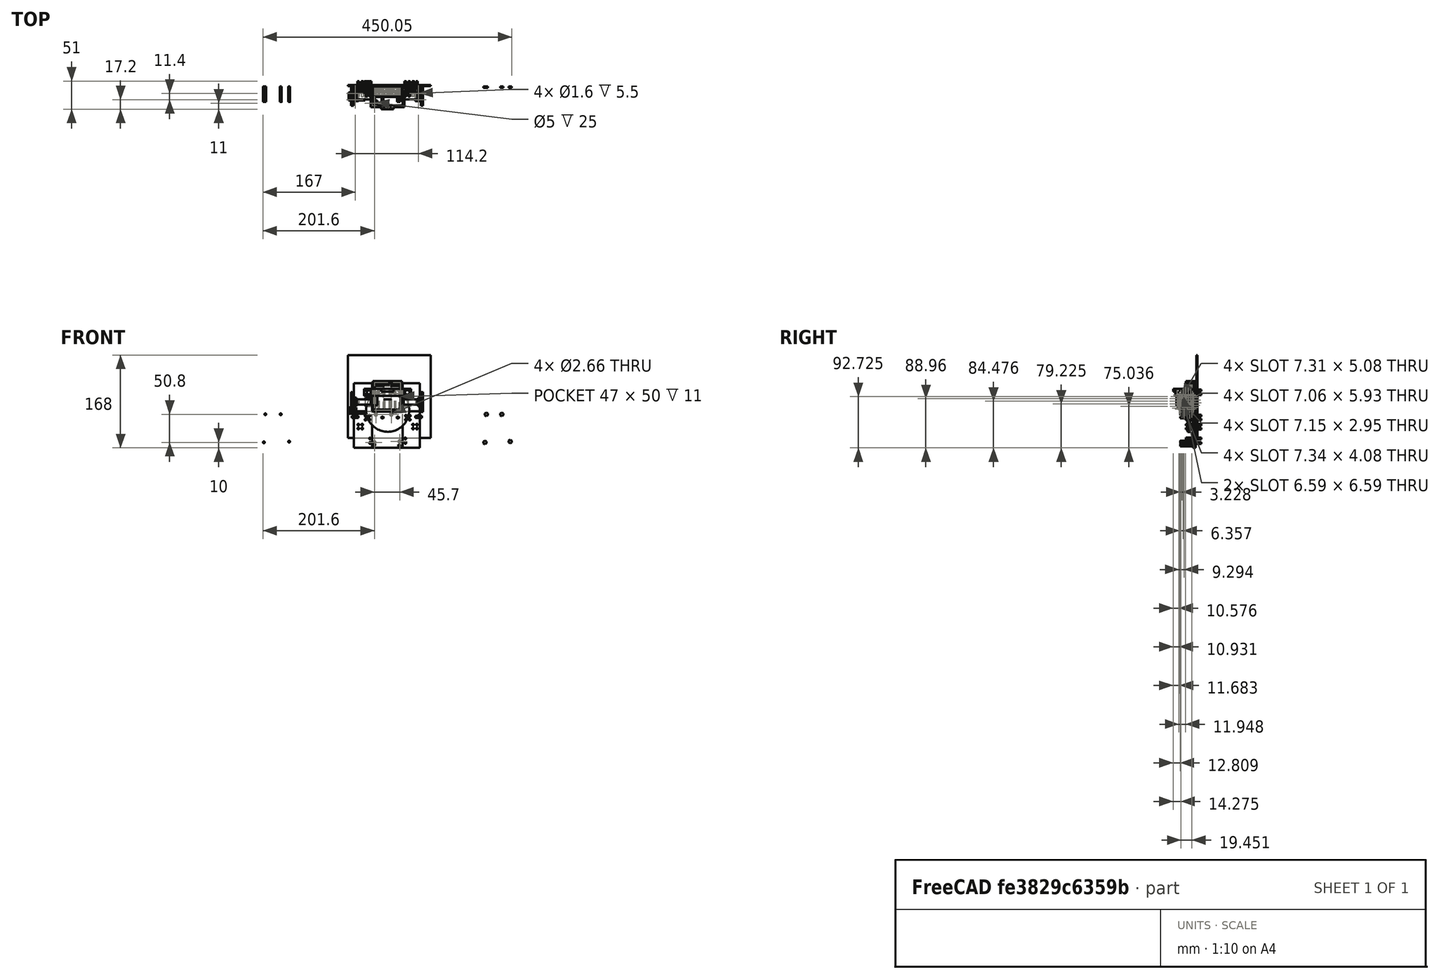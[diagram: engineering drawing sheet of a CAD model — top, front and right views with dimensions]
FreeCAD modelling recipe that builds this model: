
FCSTD DOCUMENT  (FreeCAD 0.16R6712 (Git))
Label: 5028.2 Blank Frank the Robot
License: All rights reserved
LicenseURL: http://en.wikipedia.org/wiki/All_rights_reserved
objects: Part::Cylinder×83, Part::Box×45, Part::Fuse×45, Part::Cut×39, Part::Feature×17, Part::MultiFuse×16, Part::Mirroring×6, Part::Cone×4, Part::Compound×3, Part::Torus×2, Part::Chamfer×2, App::DocumentObjectGroup×1
note: 262 computed .brp shape members not serialized (recipe doc carries the construction recipe); baked Part::Feature solids carry a one-line shape summary decoded from their .brp

FEATURE [Part::Cylinder] Cylinder
  Angle = 360
  Height = 30
  Radius = 7
FEATURE [Part::Cylinder] Cylinder001
  Angle = 360
  Height = 19
  Placement = pos=(0,0,30) rot=(0,0,1;0rad)
  Radius = 7
FEATURE [Part::Cylinder] Cylinder002
  Angle = 360
  Height = 1.8
  Placement = pos=(0,0,49) rot=(0,0,1;0rad)
  Radius = 2.5
FEATURE [Part::Compound] Compound
  Links = -> [Cylinder,Cylinder002,Cylinder001]
FEATURE [Part::Cylinder] Cylinder003
  Angle = 360
  Height = 30
  Radius = 7
FEATURE [Part::Cylinder] Cylinder004
  Angle = 360
  Height = 19
  Placement = pos=(0,0,30) rot=(0,0,1;0rad)
  Radius = 7
FEATURE [Part::Cylinder] Cylinder005
  Angle = 360
  Height = 1.8
  Placement = pos=(0,0,49) rot=(0,0,1;0rad)
  Radius = 2.5
FEATURE [Part::Compound] Compound001
  Links = -> [Cylinder003,Cylinder005,Cylinder004]
  Placement = pos=(14.5,0,50) rot=(1,0,0;3.14159rad)
FEATURE [Part::Cylinder] Cylinder006
  Angle = 360
  Height = 30
  Radius = 7
FEATURE [Part::Cylinder] Cylinder007
  Angle = 360
  Height = 19
  Placement = pos=(0,0,30) rot=(0,0,1;0rad)
  Radius = 7
FEATURE [Part::Cylinder] Cylinder008
  Angle = 360
  Height = 1.8
  Placement = pos=(0,0,49) rot=(0,0,1;0rad)
  Radius = 2.5
FEATURE [Part::Compound] Compound002
  Links = -> [Cylinder006,Cylinder008,Cylinder007]
  Placement = pos=(29,0,0) rot=(0,0,1;0rad)
FEATURE [Part::Box] Box  label="Cube"
  Height = 50
  Length = 47
  Placement = pos=(-9,-8,0) rot=(0,0,1;0rad)
  Width = 12
FEATURE [Part::Box] Box001  label="Cube001"
  Height = 55
  Length = 53
  Placement = pos=(-12,-8,-2.5) rot=(0,0,1;0rad)
  Width = 11
FEATURE [Part::Cylinder] Cylinder009
  Angle = 360
  Height = 50
  Radius = 7
FEATURE [Part::Cylinder] Cylinder010
  Angle = 360
  Height = 50
  Placement = pos=(14.5,0,0) rot=(0,0,1;0rad)
  Radius = 7
FEATURE [Part::Cut] Cut
  Base = -> Box001
  Tool = -> Box
FEATURE [Part::Box] Box002  label="Cube002"
  Height = 55
  Length = 53
  Placement = pos=(-12,3,-2.5) rot=(0,0,1;0rad)
  Width = 7
FEATURE [Part::Fuse] Fusion
  Base = -> Cut
  Tool = -> Box002
FEATURE [Part::Cut] Cut001  label="No idea why this is here...."
  Base = -> Fusion
  Tool = -> Cylinder009
FEATURE [Part::Cylinder] Cylinder011
  Angle = 360
  Height = 50
  Placement = pos=(29,0,0) rot=(0,0,1;0rad)
  Radius = 7
FEATURE [Part::Box] Box003  label="Cube003"
  Height = 5
  Length = 2
  Placement = pos=(28,-9,-2) rot=(0,0,1;0rad)
  Width = 12
FEATURE [Part::Box] Box004  label="Cube004"
  Height = 5
  Length = 2
  Placement = pos=(18.5,-9,46) rot=(0,0,1;0rad)
  Width = 12
FEATURE [Part::Box] Box005  label="Cube005"
  Height = 5
  Length = 2
  Placement = pos=(-2,-9,46) rot=(0,0,1;0rad)
  Width = 12
FEATURE [Part::Box] Box006  label="Cube006"
  Height = 5
  Length = 3
  Placement = pos=(35,-9,-4) rot=(0,0,1;0rad)
  Width = 12
FEATURE [Part::Cut] Cut008
FEATURE [Part::Torus] Torus001
  Angle1 = -180
  Angle2 = 180
  Angle3 = 360
  Placement = pos=(0,0,2) rot=(0,0,1;0rad)
  Radius1 = 19
  Radius2 = 1.5
FEATURE [Part::Cut] Cut009  label="wheel2"
  Base = -> Cut008
  Placement = pos=(75,-7,15) rot=(0,1,0;1.5708rad)
  Tool = -> Torus001
FEATURE [Part::Torus] Torus
  Angle1 = -180
  Angle2 = 180
  Angle3 = 360
  Placement = pos=(0,0,2) rot=(0,0,1;0rad)
  Radius1 = 19
  Radius2 = 1.5
FEATURE [Part::Cut] Cut010
FEATURE [Part::Cut] Cut011  label="wheel1"
  Base = -> Cut010
  Placement = pos=(-51,-7,15) rot=(0,1,0;1.5708rad)
  Tool = -> Torus
FEATURE [Part::Fuse] Fusion003
FEATURE [Part::Cylinder] Cylinder012
  Angle = 360
  Height = 10
  Placement = pos=(5,-4.5,0) rot=(0,1,0;1.5708rad)
  Radius = 0.8
FEATURE [Part::Fuse] Fusion048  label="right-motor001"
  Base = -> Cylinder012
  Placement = pos=(-51,-7,15) rot=(0,0,1;0rad)
  Tool = -> Fusion003
FEATURE [Part::Fuse] Fusion049
FEATURE [Part::Cylinder] Cylinder013
  Angle = 360
  Height = 10
  Placement = pos=(5,-4.5,0) rot=(0,1,0;1.5708rad)
  Radius = 0.8
FEATURE [Part::Fuse] Fusion050  label="left-motor001"
  Base = -> Cylinder013
  Placement = pos=(79,-7,15) rot=(0,0,1;3.14159rad)
  Tool = -> Fusion049
FEATURE [Part::Box] Box007  label="Cube007"
  Height = 5
  Length = 2
  Placement = pos=(37.5,-9,46) rot=(0,0,1;0rad)
  Width = 12
FEATURE [Part::Box] Box008  label="Cube008"
  Height = 5
  Length = 2
  Placement = pos=(8,-9,-2) rot=(0,0,1;0rad)
  Width = 12
FEATURE [Part::Box] Box009  label="The Ground"
  Height = 150
  Length = 150
  Placement = pos=(-57,11,-50) rot=(0,0,1;0rad)
  Width = 2
FEATURE [Part::Box] Box010  label="Motor Mount Left"
  Height = 16
  Length = 4
  Placement = pos=(70,-13,7) rot=(0,0,1;0rad)
  Width = 20
FEATURE [Part::Box] Box011  label="Motor Mount Right"
  Height = 16
  Length = 4
  Placement = pos=(-46,-13,7) rot=(0,0,1;0rad)
  Width = 20
FEATURE [Part::Box] Box012  label="Motor Support Right"
  Height = 16
  Length = 10
  Placement = pos=(-25,-1,7) rot=(0,0,1;0rad)
  Width = 8
FEATURE [Part::Box] Box013  label="Motor Support Left"
  Height = 16
  Length = 10
  Placement = pos=(43,-1,7) rot=(0,0,1;0rad)
  Width = 8
FEATURE [Part::Cylinder] Cylinder014
  Angle = 360
  Height = 28
  Placement = pos=(40.7,0,-10.3) rot=(1,0,0;1.5708rad)
  Radius = 1.6
FEATURE [Part::Cylinder] Cylinder015
  Angle = 360
  Height = 28
  Placement = pos=(-2.4,0,-59.8) rot=(1,0,0;1.5708rad)
  Radius = 1.6
FEATURE [Part::Cylinder] Cylinder016
  Angle = 360
  Height = 28
  Placement = pos=(-5,0,-9) rot=(1,0,0;1.5708rad)
  Radius = 1.6
FEATURE [Part::Cylinder] Cylinder017
  Angle = 360
  Height = 28
  Placement = pos=(25.5,0,-59.8) rot=(1,0,0;1.5708rad)
  Radius = 1.6
FEATURE [Part::Fuse] Fusion051
  Base = -> Cylinder015
  Tool = -> Cylinder016
FEATURE [Part::Fuse] Fusion052
  Base = -> Cylinder014
  Tool = -> Cylinder017
FEATURE [Part::Fuse] Fusion053  label="Screw holes on Arduino Duo"
  Base = -> Fusion051
  Tool = -> Fusion052
FEATURE [Part::Mirroring] Part__Mirroring  label="XXXXXScrew holes on Arduino Duo (Mirror #1)"
  Base = (0,0,0)
  Normal = (0,0,1)
  Placement = pos=(-204,10,-67) rot=(0,0,1;0rad)
  Source = -> Fusion053
FEATURE [Part::Box] Box014  label="Not used Cube"
  Height = 51
  Length = 119
  Placement = pos=(-46,7,-2) rot=(0,0,1;0rad)
  Width = 3
FEATURE [Part::Box] Box015  label="Cube014 Arduino Support cube"
  Height = 67
  Length = 55
  Placement = pos=(-13,5,-68) rot=(0,0,1;0rad)
  Width = 5
FEATURE [Part::Cylinder] Cylinder018
  Angle = 360
  Height = 5
  Placement = pos=(15,0,0) rot=(1,0,0;1.5708rad)
  Radius = 39
FEATURE [Part::Cut] Cut014  label="M3 Nut"
  Base = -> Cut001
  Placement = pos=(-6.4,10,-7.2) rot=(1,0,0;1.5708rad)
  Tool = -> Cylinder001
FEATURE [Part::Cut] Cut015  label="M3 Nut001"
  Base = -> Cut001
  Placement = pos=(21.5,10,-7.2) rot=(1,0,0;1.5708rad)
  Tool = -> Cylinder001
FEATURE [Part::Cut] Cut016  label="M3 Nut002"
  Base = -> Cut001
  Placement = pos=(36.7,10,-56.7) rot=(1,0,0;1.5708rad)
  Tool = -> Cylinder001
FEATURE [Part::Cut] Cut017  label="M3 Nut003"
  Base = -> Cut001
  Placement = pos=(-9,10,-58) rot=(1,0,0;1.5708rad)
  Tool = -> Cylinder001
FEATURE [Part::Cut] Cut018
  Base = -> Cut
  Placement = pos=(-9,10,-58) rot=(1,0,0;1.5708rad)
  Tool = -> Box006
FEATURE [Part::Cut] Cut019
  Base = -> Cut
  Placement = pos=(36.7,10,-56.7) rot=(1,0,0;1.5708rad)
  Tool = -> Box006
FEATURE [Part::Cut] Cut020
  Base = -> Cut
  Placement = pos=(-6.4,10,-7.2) rot=(1,0,0;1.5708rad)
  Tool = -> Box006
FEATURE [Part::Cut] Cut021
  Base = -> Cut
  Placement = pos=(21.5,10,-7.2) rot=(1,0,0;1.5708rad)
  Tool = -> Box006
FEATURE [Part::MultiFuse] Fusion054  label="XXXXXHex Holes"
  Placement = pos=(200,0,0) rot=(0,0,1;0rad)
  Shapes = -> [Cut018,Cut021,Cut019,Cut020]
FEATURE [Part::Box] Box016  label="Cube015"
  Height = 117
  Length = 33
  Placement = pos=(-46,7,-68) rot=(0,0,1;0rad)
  Width = 3
FEATURE [Part::Box] Box017  label="Cube016"
  Height = 117
  Length = 31
  Placement = pos=(42,7,-68) rot=(0,0,1;0rad)
  Width = 3
FEATURE [Part::Cylinder] Cylinder019
  Angle = 360
  Height = 28
  Placement = pos=(48,20,-10) rot=(1,0,0;1.5708rad)
  Radius = 1.6
FEATURE [Part::Cylinder] Cylinder020
  Angle = 360
  Height = 28
  Placement = pos=(47,20,-51) rot=(1,0,0;1.5708rad)
  Radius = 1.6
FEATURE [Part::Cylinder] Cylinder021
  Angle = 360
  Height = 28
  Placement = pos=(48,20,-17) rot=(1,0,0;1.5708rad)
  Radius = 1.6
FEATURE [Part::Cylinder] Cylinder022
  Angle = 360
  Height = 28
  Placement = pos=(47,20,-59) rot=(1,0,0;1.5708rad)
  Radius = 1.6
FEATURE [Part::Cylinder] Cylinder023
  Angle = 360
  Height = 28
  Placement = pos=(55,20,-17) rot=(1,0,0;1.5708rad)
  Radius = 1.6
FEATURE [Part::Cylinder] Cylinder024
  Angle = 360
  Height = 28
  Placement = pos=(55,20,-10) rot=(1,0,0;1.5708rad)
  Radius = 1.6
FEATURE [Part::MultiFuse] Fusion055
  Shapes = -> [Cylinder021,Cylinder023,Cylinder024,Cylinder019]
FEATURE [Part::MultiFuse] Fusion056
  Placement = pos=(13,0,-16) rot=(0,0,1;0rad)
  Shapes = -> [Cylinder021,Cylinder023,Cylinder024,Cylinder019]
FEATURE [Part::MultiFuse] Fusion057  label="Mount holes top left"
  Placement = pos=(-1,0,46) rot=(0,0,1;0rad)
  Shapes = -> [Cylinder021,Cylinder023,Cylinder024,Cylinder019]
FEATURE [Part::MultiFuse] Fusion058  label="Mount holes top right"
  Placement = pos=(-71,0,46) rot=(0,0,1;0rad)
  Shapes = -> [Cylinder021,Cylinder023,Cylinder024,Cylinder019]
FEATURE [Part::MultiFuse] Fusion059
  Shapes = -> [Cylinder022,Cylinder020,Fusion055,Fusion056]
FEATURE [Part::Mirroring] Part__Mirroring001  label="Mount holes bottom right"
  Base = (0,0,0)
  Normal = (1,0,0)
  Placement = pos=(30,0,0) rot=(0,0,1;0rad)
  Source = -> Fusion059
FEATURE [Part::Cylinder] Cylinder025
  Angle = 360
  Height = 28
  Placement = pos=(48,20,-10) rot=(1,0,0;1.5708rad)
  Radius = 1.6
FEATURE [Part::Cylinder] Cylinder026
  Angle = 360
  Height = 28
  Placement = pos=(47,20,-51) rot=(1,0,0;1.5708rad)
  Radius = 1.6
FEATURE [Part::Cylinder] Cylinder027
  Angle = 360
  Height = 28
  Placement = pos=(48,20,-17) rot=(1,0,0;1.5708rad)
  Radius = 1.6
FEATURE [Part::Cylinder] Cylinder028
  Angle = 360
  Height = 28
  Placement = pos=(47,20,-59) rot=(1,0,0;1.5708rad)
  Radius = 1.6
FEATURE [Part::Cylinder] Cylinder029
  Angle = 360
  Height = 28
  Placement = pos=(55,20,-17) rot=(1,0,0;1.5708rad)
  Radius = 1.6
FEATURE [Part::Cylinder] Cylinder030
  Angle = 360
  Height = 28
  Placement = pos=(55,20,-10) rot=(1,0,0;1.5708rad)
  Radius = 1.6
FEATURE [Part::MultiFuse] Fusion060
  Shapes = -> [Cylinder027,Cylinder029,Cylinder030,Cylinder025]
FEATURE [Part::MultiFuse] Fusion061
  Placement = pos=(13,0,-16) rot=(0,0,1;0rad)
  Shapes = -> [Cylinder027,Cylinder029,Cylinder030,Cylinder025]
FEATURE [Part::MultiFuse] Fusion062  label="Mount holes bottom left"
  Shapes = -> [Cylinder028,Cylinder026,Fusion060,Fusion061]
FEATURE [Part::Cylinder] Cylinder031  label="Cylinder083"
  Angle = 360
  Height = 10
  Placement = pos=(0,18,29) rot=(0,0,1;0rad)
  Radius = 2.25
FEATURE [Part::Cylinder] Cylinder032  label="Cylinder084"
  Angle = 360
  Height = 10
  Placement = pos=(4.5,18,32) rot=(0,0,1;0rad)
  Radius = 1
FEATURE [Part::Cylinder] Cylinder033  label="Cylinder085"
  Angle = 360
  Height = 10
  Placement = pos=(-4.5,18,32) rot=(0,0,1;0rad)
  Radius = 1
FEATURE [Part::Fuse] Fusion009  label="Mounting Screw Holes"
  Base = -> Cylinder032
  Tool = -> Cylinder033
FEATURE [Part::Fuse] Fusion071  label="Motor Holes Left"
  Base = -> Cylinder031
  Placement = pos=(37,-7,-3) rot=(0.57735,0.57735,0.57735;2.0944rad)
  Tool = -> Fusion009
FEATURE [Part::Cylinder] Cylinder034  label="Cylinder086"
  Angle = 360
  Height = 10
  Placement = pos=(0,18,29) rot=(0,0,1;0rad)
  Radius = 2.25
FEATURE [Part::Cylinder] Cylinder035  label="Cylinder087"
  Angle = 360
  Height = 10
  Placement = pos=(4.5,18,32) rot=(0,0,1;0rad)
  Radius = 1
FEATURE [Part::Cylinder] Cylinder036  label="Cylinder088"
  Angle = 360
  Height = 10
  Placement = pos=(-4.5,18,32) rot=(0,0,1;0rad)
  Radius = 1
FEATURE [Part::Fuse] Fusion072  label="Mounting Screw Holes001"
  Base = -> Cylinder035
  Tool = -> Cylinder036
FEATURE [Part::Fuse] Fusion073  label="Motor Holes Right"
  Base = -> Cylinder034
  Placement = pos=(-79,-7,-3) rot=(0.57735,0.57735,0.57735;2.0944rad)
  Tool = -> Fusion072
FEATURE [Part::Cylinder] Cylinder037  label="Cylinder089"
  Angle = 360
  Height = 28
  Placement = pos=(40.7,0,-10.3) rot=(1,0,0;1.5708rad)
  Radius = 1.6
FEATURE [Part::Cylinder] Cylinder038  label="Cylinder090"
  Angle = 360
  Height = 28
  Placement = pos=(-2.4,0,-59.8) rot=(1,0,0;1.5708rad)
  Radius = 1.6
FEATURE [Part::Cylinder] Cylinder039  label="Cylinder091"
  Angle = 360
  Height = 28
  Placement = pos=(-5,0,-9) rot=(1,0,0;1.5708rad)
  Radius = 1.6
FEATURE [Part::Cylinder] Cylinder040  label="Cylinder092"
  Angle = 360
  Height = 28
  Placement = pos=(25.5,0,-59.8) rot=(1,0,0;1.5708rad)
  Radius = 1.6
FEATURE [Part::Fuse] Fusion074
  Base = -> Cylinder038
  Tool = -> Cylinder039
FEATURE [Part::Fuse] Fusion075
  Base = -> Cylinder037
  Tool = -> Cylinder040
FEATURE [Part::Fuse] Fusion076  label="Screw holes on Arduino Duo001"
  Base = -> Fusion074
  Tool = -> Fusion075
FEATURE [Part::Mirroring] Part__Mirroring002  label="Screw holes on Arduino Duo (Mirror #1)001"
  Base = (0,0,0)
  Normal = (0,0,1)
  Placement = pos=(-4,10,-67) rot=(0,0,1;0rad)
  Source = -> Fusion076
FEATURE [Part::Mirroring] Part__Mirroring003  label="Screw holes on Arduino Duo (Mirror #1)001 (Mirror #4)"
  Base = (0,0,0)
  Normal = (1,0,0)
  Placement = pos=(27,0,-6) rot=(0,0,1;0rad)
  Source = -> Part__Mirroring002
FEATURE [Part::Box] Box018  label="Cube017"
  Height = 50
  Length = 47
  Placement = pos=(-9,-8,0) rot=(0,0,1;0rad)
  Width = 12
FEATURE [Part::Box] Box019  label="Cube018"
  Height = 55
  Length = 53
  Placement = pos=(-12,-8,-2.5) rot=(0,0,1;0rad)
  Width = 11
FEATURE [Part::Cut] Cut031
  Base = -> Box019
  Tool = -> Box018
FEATURE [Part::Box] Box020  label="Cube019"
  Height = 5
  Length = 3
  Placement = pos=(35,-9,-4) rot=(0,0,1;0rad)
  Width = 12
FEATURE [Part::Cut] Cut032
  Base = -> Cut031
  Placement = pos=(-9,10,-58) rot=(1,0,0;1.5708rad)
  Tool = -> Box020
FEATURE [Part::Cut] Cut033
  Base = -> Cut031
  Placement = pos=(36.7,10,-56.7) rot=(1,0,0;1.5708rad)
  Tool = -> Box020
FEATURE [Part::Cut] Cut034
  Base = -> Cut031
  Placement = pos=(-6.4,10,-7.2) rot=(1,0,0;1.5708rad)
  Tool = -> Box020
FEATURE [Part::Cut] Cut035
  Base = -> Cut031
  Placement = pos=(21.5,10,-7.2) rot=(1,0,0;1.5708rad)
  Tool = -> Box020
FEATURE [Part::MultiFuse] Fusion077
  Shapes = -> [Cut032,Cut035,Cut033,Cut034]
FEATURE [Part::Mirroring] Part__Mirroring004  label="Hex Holes"
  Base = (0,0,0)
  Normal = (1,0,0)
  Placement = pos=(27,0,-6) rot=(0,0,1;0rad)
  Source = -> Fusion077
FEATURE [Part::Box] Box021  label="Cube020"
  Height = 13
  Length = 61
  Placement = pos=(-16,-27,26) rot=(0,0,1;0rad)
  Width = 34
FEATURE [Part::Box] Box022  label="Cube021"
  Height = 13
  Length = 12
  Placement = pos=(45,4,26) rot=(0,0,1;0rad)
  Width = 3
FEATURE [Part::Box] Box023  label="Cube022"
  Height = 13
  Length = 12
  Placement = pos=(-28,4,26) rot=(0,0,1;0rad)
  Width = 3
FEATURE [Part::Box] Box024  label="Cube023"
  Height = 13
  Length = 55
  Placement = pos=(-13,-24,26) rot=(0,0,1;0rad)
  Width = 31
FEATURE [Part::Cylinder] Cylinder041  label="Cylinder093"
  Angle = 360
  Height = 28
  Placement = pos=(54,20,29) rot=(1,0,0;1.5708rad)
  Radius = 1.6
FEATURE [Part::Cylinder] Cylinder042  label="Cylinder094"
  Angle = 360
  Height = 28
  Placement = pos=(54,20,36) rot=(1,0,0;1.5708rad)
  Radius = 1.6
FEATURE [Part::Cylinder] Cylinder043  label="Cylinder095"
  Angle = 360
  Height = 28
  Placement = pos=(-23,20,29) rot=(1,0,0;1.5708rad)
  Radius = 1.6
FEATURE [Part::Cylinder] Cylinder044  label="Cylinder096"
  Angle = 360
  Height = 28
  Placement = pos=(-23,20,36) rot=(1,0,0;1.5708rad)
  Radius = 1.6
FEATURE [Part::Cylinder] Cylinder045  label="Cylinder097"
  Angle = 360
  Height = 10
  Placement = pos=(36,-17.25,32.5) rot=(0,1,0;1.5708rad)
  Radius = 3.25
FEATURE [Part::Cut] Cut037
  Base = -> Box021
  Tool = -> Box024
FEATURE [Part::Cut] Cut038
  Base = -> Cut037
  Tool = -> Cylinder045
FEATURE [Part::Box] Box025  label="Cube024"
  Height = 5
  Length = 22
  Placement = pos=(3.5,-31,34) rot=(0,0,1;0rad)
  Width = 4
FEATURE [Part::Cylinder] Cylinder046  label="Cylinder098"
  Angle = 360
  Height = 10
  Placement = pos=(20.65,-29,30) rot=(0,0,1;0rad)
  Radius = 0.85
FEATURE [Part::Cylinder] Cylinder047  label="Cylinder099"
  Angle = 360
  Height = 10
  Placement = pos=(8.35,-29,40) rot=(1,0,0;3.14159rad)
  Radius = 0.85
FEATURE [Part::Fuse] Fusion078
  Base = -> Cylinder046
  Tool = -> Cylinder047
FEATURE [Part::Cut] Cut039
  Base = -> Box025
  Tool = -> Fusion078
FEATURE [Part::Fuse] Fusion079
  Base = -> Cut038
  Tool = -> Cut039
FEATURE [Part::Fuse] Fusion080
  Base = -> Cylinder043
  Tool = -> Cylinder044
FEATURE [Part::Fuse] Fusion081
  Base = -> Cylinder041
  Tool = -> Cylinder042
FEATURE [Part::Fuse] Fusion082
  Base = -> Box023
  Tool = -> Fusion079
FEATURE [Part::Fuse] Fusion083
  Base = -> Box022
  Tool = -> Fusion082
FEATURE [Part::Cut] Cut040
  Base = -> Fusion083
  Tool = -> Fusion081
FEATURE [Part::Cut] Cut041  label="Switch Bracket"
  Base = -> Cut040
  Tool = -> Fusion080
FEATURE [Part::Cylinder] Cylinder048  label="Cylinder100"
  Angle = 360
  Height = 28
  Placement = pos=(-23,20,29) rot=(1,0,0;1.5708rad)
  Radius = 1.6
FEATURE [Part::Cylinder] Cylinder049  label="Cylinder101"
  Angle = 360
  Height = 28
  Placement = pos=(-23,20,36) rot=(1,0,0;1.5708rad)
  Radius = 1.6
FEATURE [Part::Fuse] Fusion084
  Base = -> Cylinder048
  Placement = pos=(1,0,0) rot=(0,0,1;0rad)
  Tool = -> Cylinder049
FEATURE [Part::Cylinder] Cylinder050  label="Cylinder102"
  Angle = 360
  Height = 28
  Placement = pos=(-23,20,29) rot=(1,0,0;1.5708rad)
  Radius = 1.6
FEATURE [Part::Cylinder] Cylinder051  label="Cylinder103"
  Angle = 360
  Height = 28
  Placement = pos=(-23,20,36) rot=(1,0,0;1.5708rad)
  Radius = 1.6
FEATURE [Part::Fuse] Fusion085
  Base = -> Cylinder050
  Placement = pos=(-1,0,0) rot=(0,0,1;0rad)
  Tool = -> Cylinder051
FEATURE [Part::Cut] Cut042
  Base = -> Cut041
  Tool = -> Fusion084
FEATURE [Part::Cut] Cut043  label="Switch Bracket001"
  Base = -> Cut042
  Tool = -> Fusion085
FEATURE [Part::Cylinder] Cylinder052  label="Cylinder104"
  Angle = 360
  Height = 42
  Radius = 4.8
FEATURE [Part::Cylinder] Cylinder053  label="Cylinder105"
  Angle = 360
  Height = 1.6
  Placement = pos=(0,0,42) rot=(0,0,1;0rad)
  Radius = 1.65
FEATURE [Part::Fuse] Fusion086
  Base = -> Cylinder052
  Placement = pos=(2,0,0) rot=(0,0,1;0rad)
  Tool = -> Cylinder053
FEATURE [Part::Cylinder] Cylinder054  label="Cylinder106"
  Angle = 360
  Height = 42
  Radius = 4.8
FEATURE [Part::Cylinder] Cylinder055  label="Cylinder107"
  Angle = 360
  Height = 1.6
  Placement = pos=(0,0,42) rot=(0,0,1;0rad)
  Radius = 1.65
FEATURE [Part::Fuse] Fusion087
  Base = -> Cylinder054
  Placement = pos=(12,0,0) rot=(0,0,1;0rad)
  Tool = -> Cylinder055
FEATURE [Part::Cylinder] Cylinder056  label="Cylinder108"
  Angle = 360
  Height = 42
  Radius = 4.8
FEATURE [Part::Cylinder] Cylinder057  label="Cylinder109"
  Angle = 360
  Height = 1.6
  Placement = pos=(0,0,42) rot=(0,0,1;0rad)
  Radius = 1.65
FEATURE [Part::Fuse] Fusion088
  Base = -> Cylinder056
  Placement = pos=(22,0,0) rot=(0,0,1;0rad)
  Tool = -> Cylinder057
FEATURE [Part::Cylinder] Cylinder058  label="Cylinder110"
  Angle = 360
  Height = 42
  Radius = 4.8
FEATURE [Part::Cylinder] Cylinder059  label="Cylinder111"
  Angle = 360
  Height = 1.6
  Placement = pos=(0,0,42) rot=(0,0,1;0rad)
  Radius = 1.65
FEATURE [Part::Fuse] Fusion089
  Base = -> Cylinder058
  Placement = pos=(32,0,0) rot=(0,0,1;0rad)
  Tool = -> Cylinder059
FEATURE [Part::Cylinder] Cylinder060  label="Cylinder112"
  Angle = 360
  Height = 42
  Radius = 4.8
FEATURE [Part::Cylinder] Cylinder061  label="Cylinder113"
  Angle = 360
  Height = 1.6
  Placement = pos=(0,0,42) rot=(0,0,1;0rad)
  Radius = 1.65
FEATURE [Part::Fuse] Fusion093
  Base = -> Cylinder060
  Placement = pos=(-8,0,0) rot=(0,0,1;0rad)
  Tool = -> Cylinder061
FEATURE [Part::MultiFuse] Fusion094  label="AAA Batts"
  Placement = pos=(2.5,0,2) rot=(0,0,1;0rad)
  Shapes = -> [Fusion093,Fusion086,Fusion087,Fusion088,Fusion089]
FEATURE [Part::Cylinder] Cylinder062  label="Cylinder114"
  Angle = 360
  Height = 10
  Radius = 17
FEATURE [Part::Cylinder] Cylinder063  label="Cylinder115"
  Angle = 360
  Height = 16
  Placement = pos=(0,0,-4) rot=(0,0,1;0rad)
  Radius = 10
FEATURE [Part::Cut] Cut044
  Base = -> Cylinder062
  Tool = -> Cylinder063
FEATURE [Part::Box] Box026  label="Cube025"
  Height = 20
  Length = 18
  Placement = pos=(0,0,-5) rot=(0,0,1;0rad)
  Width = 20
FEATURE [Part::Box] Box027  label="Cube026"
  Height = 20
  Length = 10
  Placement = pos=(0,0,-5) rot=(0,0,1;0.174533rad)
  Width = 20
FEATURE [Part::Cut] Cut045
  Base = -> Box027
  Tool = -> Box026
FEATURE [Part::Feature] Cut045001
  Placement = pos=(0,0,0) rot=(0,0,1;0.349066rad)
  shape: bbox 10 x 22.32 x 20 mm, 7 faces (baked)
FEATURE [Part::Feature] Cut045002
  Placement = pos=(0,0,0) rot=(0,0,1;0.698132rad)
  shape: bbox 15.32 x 20.52 x 20 mm, 7 faces (baked)
FEATURE [Part::Feature] Cut045003
  Placement = pos=(0,0,0) rot=(0,0,1;1.0472rad)
  shape: bbox 18.79 x 16.24 x 20 mm, 7 faces (baked)
FEATURE [Part::Feature] Cut045004
  Placement = pos=(0,0,0) rot=(0,0,1;1.39626rad)
  shape: bbox 20 x 10 x 20 mm, 7 faces (baked)
FEATURE [Part::Feature] Cut045005
  Placement = pos=(0,0,0) rot=(0,0,1;1.74533rad)
  shape: bbox 22.21 x 9.894 x 20 mm, 7 faces (baked)
FEATURE [Part::Feature] Cut045006
  Placement = pos=(0,0,0) rot=(0,0,1;2.0944rad)
  shape: bbox 21.75 x 12.86 x 20 mm, 7 faces (baked)
FEATURE [Part::Feature] Cut045007
  Placement = pos=(0,0,0) rot=(0,0,1;2.44346rad)
  shape: bbox 18.66 x 17.32 x 20 mm, 7 faces (baked)
FEATURE [Part::Feature] Cut045008
  Placement = pos=(0,0,0) rot=(0,0,1;2.79253rad)
  shape: bbox 13.32 x 19.7 x 20 mm, 7 faces (baked)
FEATURE [Part::Feature] Cut045009
  Placement = pos=(0,0,0) rot=(0,0,1;3.14159rad)
  shape: bbox 10.1 x 21.43 x 20 mm, 7 faces (baked)
FEATURE [Part::Feature] Cut045010
  Placement = pos=(0,0,0) rot=(0,0,1;3.49066rad)
  shape: bbox 10 x 22.32 x 20 mm, 7 faces (baked)
FEATURE [Part::Feature] Cut045011
  Placement = pos=(0,0,0) rot=(0,0,1;3.83972rad)
  shape: bbox 15.32 x 20.52 x 20 mm, 7 faces (baked)
FEATURE [Part::Feature] Cut045012
  Placement = pos=(0,0,0) rot=(0,0,1;4.18879rad)
  shape: bbox 18.79 x 16.24 x 20 mm, 7 faces (baked)
FEATURE [Part::Feature] Cut045013
  Placement = pos=(0,0,0) rot=(0,0,-1;1.74533rad)
  shape: bbox 20 x 10 x 20 mm, 7 faces (baked)
FEATURE [Part::Feature] Cut045014
  Placement = pos=(0,0,0) rot=(0,0,-1;1.39626rad)
  shape: bbox 22.21 x 9.894 x 20 mm, 7 faces (baked)
FEATURE [Part::Feature] Cut045015
  Placement = pos=(0,0,0) rot=(0,0,-1;1.0472rad)
  shape: bbox 21.75 x 12.86 x 20 mm, 7 faces (baked)
FEATURE [Part::Feature] Cut045016
  Placement = pos=(0,0,0) rot=(0,0,-1;0.698132rad)
  shape: bbox 18.66 x 17.32 x 20 mm, 7 faces (baked)
FEATURE [Part::Feature] Cut045017
  Placement = pos=(0,0,0) rot=(0,0,-1;0.349066rad)
  shape: bbox 13.32 x 19.7 x 20 mm, 7 faces (baked)
FEATURE [Part::MultiFuse] Fusion095
  Shapes = -> [Cut045001,Cut045008,Cut045010,Cut045009,Cut045005,Cut045003,Cut045006,Cut045002,Cut045004,Cut045007,Cut045016,Cut045017,Cut045011,Cut045012,Cut045013,Cut045014,Cut045015,Cut045]
FEATURE [Part::Cut] Cut045018
  Base = -> Cut044
  Placement = pos=(72,-7,15) rot=(0,1,0;1.5708rad)
  Tool = -> Fusion095
FEATURE [Part::Cut] Cut045019  label="Wheel with Spokes AB"
  Base = -> Cut009
  Tool = -> Cut045018
FEATURE [Part::Box] Box028  label="Cube027"
  Height = 5
  Length = 2
  Placement = pos=(37.5,-9,-2) rot=(0,0,1;0rad)
  Width = 12
FEATURE [Part::Box] Box029  label="Cube028"
  Height = 50
  Length = 47
  Placement = pos=(-9,-8,0) rot=(0,0,1;0rad)
  Width = 12
FEATURE [Part::Box] Box030  label="Cube029"
  Height = 55
  Length = 53
  Placement = pos=(-12,-8,-2.5) rot=(0,0,1;0rad)
  Width = 11
FEATURE [Part::Cylinder] Cylinder064  label="Cylinder116"
  Angle = 360
  Height = 50
  Radius = 7
FEATURE [Part::Cut] Cut045020
  Base = -> Box030
  Tool = -> Box029
FEATURE [Part::Box] Box031  label="Cube030"
  Height = 55
  Length = 53
  Placement = pos=(-12,3,-2.5) rot=(0,0,1;0rad)
  Width = 7
FEATURE [Part::Fuse] Fusion096
  Base = -> Cut045020
  Tool = -> Box031
FEATURE [App::DocumentObjectGroup] Group  label="Older version parts"
  Group = -> [Compound,Compound001,Compound002,Cylinder064,Cylinder010,Cylinder011,Fusion096,Part__Mirroring,Fusion054]
FEATURE [Part::Box] Box032  label="Battery Base"
  Height = 50
  Length = 55
  Placement = pos=(-13,3,-1) rot=(0,0,1;0rad)
  Width = 7
FEATURE [Part::Box] Box033  label="Cube031"
  Height = 30
  Length = 10
  Placement = pos=(-14,-25,9) rot=(0,0,1;0rad)
  Width = 10
FEATURE [Part::Cylinder] Cylinder065  label="Cylinder117"
  Angle = 360
  Height = 42
  Radius = 4.8
FEATURE [Part::Cylinder] Cylinder066  label="Cylinder118"
  Angle = 360
  Height = 1.6
  Placement = pos=(0,0,42) rot=(0,0,1;0rad)
  Radius = 1.65
FEATURE [Part::Fuse] Fusion097
  Base = -> Cylinder065
  Placement = pos=(2,0,0) rot=(0,0,1;0rad)
  Tool = -> Cylinder066
FEATURE [Part::Cylinder] Cylinder067  label="Cylinder119"
  Angle = 360
  Height = 42
  Radius = 4.8
FEATURE [Part::Cylinder] Cylinder068  label="Cylinder120"
  Angle = 360
  Height = 1.6
  Placement = pos=(0,0,42) rot=(0,0,1;0rad)
  Radius = 1.65
FEATURE [Part::Fuse] Fusion098
  Base = -> Cylinder067
  Placement = pos=(12,0,0) rot=(0,0,1;0rad)
  Tool = -> Cylinder068
FEATURE [Part::Cylinder] Cylinder069  label="Cylinder121"
  Angle = 360
  Height = 42
  Radius = 4.8
FEATURE [Part::Cylinder] Cylinder070  label="Cylinder122"
  Angle = 360
  Height = 1.6
  Placement = pos=(0,0,42) rot=(0,0,1;0rad)
  Radius = 1.65
FEATURE [Part::Fuse] Fusion099
  Base = -> Cylinder069
  Placement = pos=(22,0,0) rot=(0,0,1;0rad)
  Tool = -> Cylinder070
FEATURE [Part::Cylinder] Cylinder071  label="Cylinder123"
  Angle = 360
  Height = 42
  Radius = 4.8
FEATURE [Part::Cylinder] Cylinder072  label="Cylinder124"
  Angle = 360
  Height = 1.6
  Placement = pos=(0,0,42) rot=(0,0,1;0rad)
  Radius = 1.65
FEATURE [Part::Fuse] Fusion100
  Base = -> Cylinder071
  Placement = pos=(32,0,0) rot=(0,0,1;0rad)
  Tool = -> Cylinder072
FEATURE [Part::Cylinder] Cylinder073  label="Cylinder125"
  Angle = 360
  Height = 42
  Radius = 4.8
FEATURE [Part::Cylinder] Cylinder074  label="Cylinder126"
  Angle = 360
  Height = 1.6
  Placement = pos=(0,0,42) rot=(0,0,1;0rad)
  Radius = 1.65
FEATURE [Part::Fuse] Fusion101
  Base = -> Cylinder073
  Placement = pos=(-8,0,0) rot=(0,0,1;0rad)
  Tool = -> Cylinder074
FEATURE [Part::MultiFuse] Fusion102  label="AAA Batts001"
  Placement = pos=(2,0,2) rot=(0,0,1;0rad)
  Shapes = -> [Fusion101,Fusion097,Fusion098,Fusion099,Fusion100]
FEATURE [Part::Cylinder] Cylinder075  label="Cylinder127"
  Angle = 360
  Height = 10
  Placement = pos=(-9,-20,4) rot=(0,0,1;0rad)
  Radius = 2.75
FEATURE [Part::Cylinder] Cylinder076  label="Cylinder128"
  Angle = 360
  Height = 27
  Placement = pos=(-9,-20,14) rot=(0,0,1;0rad)
  Radius = 2.5
FEATURE [Part::Fuse] Fusion103  label="phototransistor hole"
  Base = -> Cylinder075
  Tool = -> Cylinder076
FEATURE [Part::Cut] Cut045021
  Base = -> Box033
  Tool = -> Fusion103
FEATURE [Part::Fuse] Fusion104  label="Switch Mount with phototransistor hole"
  Base = -> Cut043
  Tool = -> Cut045021
FEATURE [Part::Cut] Cut045022
  Base = -> Box032
  Tool = -> Fusion102
FEATURE [Part::Box] Box034  label="Cube032"
  Height = 2.5
  Length = 55
  Placement = pos=(-13,-9,-1) rot=(0,0,1;0rad)
  Width = 12
FEATURE [Part::Box] Box035  label="Cube033"
  Height = 2.5
  Length = 55
  Placement = pos=(-13,-9,46.5) rot=(0,0,1;0rad)
  Width = 12
FEATURE [Part::Box] Box036  label="Cube034"
  Height = 50
  Length = 2.5
  Placement = pos=(-13,-9,-1) rot=(0,0,1;0rad)
  Width = 12
FEATURE [Part::Box] Box037  label="Cube035"
  Height = 50
  Length = 2.5
  Placement = pos=(39.5,-9,-1) rot=(0,0,1;0rad)
  Width = 12
FEATURE [Part::MultiFuse] Fusion105
  Shapes = -> [Box034,Box036,Box037,Box035]
FEATURE [Part::Box] Box038  label="Cube036"
  Height = 5
  Length = 2
  Placement = pos=(-10.5,-9,46) rot=(0,0,1;0rad)
  Width = 12
FEATURE [Part::Box] Box039  label="Cube037"
  Height = 5
  Length = 2
  Placement = pos=(-10.5,-9,-2) rot=(0,0,1;0rad)
  Width = 12
FEATURE [Part::MultiFuse] Fusion106
  Shapes = -> [Box039,Box038,Box028,Box007]
FEATURE [Part::MultiFuse] Fusion107
  Shapes = -> [Box003,Box004,Box005,Box008]
FEATURE [Part::Cut] Cut045023
  Base = -> Fusion105
  Tool = -> Fusion106
FEATURE [Part::Cut] Cut045024
  Base = -> Cut045023
  Tool = -> Fusion107
FEATURE [Part::Box] Box040  label="Cube038"
  Height = 1.6
  Length = 30
  Placement = pos=(-56,-15.5,-6) rot=(0,0,1;0rad)
  Width = 15
FEATURE [Part::Box] Box041  label="Cube039"
  Height = 10
  Length = 14
  Placement = pos=(-56,-10.5,-4.5) rot=(0,0,1;0rad)
  Width = 6
FEATURE [Part::Box] Box042  label="Cube040"
  Height = 10
  Length = 5.3
  Placement = pos=(-51.7,-11.5,-4.5) rot=(0,0,1;0rad)
  Width = 8
FEATURE [Part::Cut] Cut045025
  Base = -> Box041
  Tool = -> Box042
FEATURE [Part::Fuse] Fusion108  label="Spoke Sensor PCB"
  Base = -> Box040
  Tool = -> Cut045025
FEATURE [Part::Cylinder] Cylinder077  label="Cylinder129"
  Angle = 360
  Height = 14.5
  Placement = pos=(-43.6,-2.4,-9) rot=(0,0,1;0rad)
  Radius = 0.8
FEATURE [Part::Cylinder] Cylinder078  label="Cylinder130"
  Angle = 360
  Height = 14.5
  Placement = pos=(-43.6,-13.8,-9) rot=(0,0,1;0rad)
  Radius = 0.8
FEATURE [Part::Fuse] Fusion109
  Base = -> Cylinder077
  Tool = -> Cylinder078
FEATURE [Part::Cut] Cut045026  label="Spoke Sensor PCB001"
  Base = -> Fusion108
  Tool = -> Fusion109
FEATURE [Part::Cylinder] Cylinder079  label="Cylinder131"
  Angle = 360
  Height = 14.5
  Placement = pos=(-43.6,-2.4,-15) rot=(0,0,1;0rad)
  Radius = 0.8
FEATURE [Part::Cylinder] Cylinder080  label="Cylinder132"
  Angle = 360
  Height = 14.5
  Placement = pos=(-43.6,-13.8,-15) rot=(0,0,1;0rad)
  Radius = 0.8
FEATURE [Part::Fuse] Fusion110
  Base = -> Cut045022
  Tool = -> Cut045024
FEATURE [Part::Box] Box043  label="Cube041"
  Height = 4
  Length = 12
  Placement = pos=(-50,-16.75,-14) rot=(0,0,1;0rad)
  Width = 26.75
FEATURE [Part::Chamfer] Chamfer
  Base = -> Box043
  Edges = 1 edges r=7: [Edge3]
FEATURE [Part::Cone] Cone
  Angle = 360
  Height = 1.5
  Placement = pos=(-43.6,-2.4,-10) rot=(0,0,1;0rad)
  Radius1 = 2.75
  Radius2 = 1.25
FEATURE [Part::Cone] Cone001
  Angle = 360
  Height = 1.5
  Placement = pos=(-43.6,-13.8,-10) rot=(0,0,1;0rad)
  Radius1 = 2.75
  Radius2 = 1.25
FEATURE [Part::Fuse] Fusion111
  Base = -> Cone
  Tool = -> Cone001
FEATURE [Part::Fuse] Fusion112
  Base = -> Chamfer
  Tool = -> Fusion111
FEATURE [Part::Fuse] Fusion113
  Base = -> Cylinder079
  Tool = -> Cylinder080
FEATURE [Part::Cut] Cut045027
  Base = -> Fusion112
  Tool = -> Fusion113
FEATURE [Part::Cylinder] Cylinder081  label="Cylinder133"
  Angle = 360
  Height = 14.5
  Placement = pos=(-43.6,-2.4,-15) rot=(0,0,1;0rad)
  Radius = 0.8
FEATURE [Part::Cylinder] Cylinder082  label="Cylinder134"
  Angle = 360
  Height = 14.5
  Placement = pos=(-43.6,-13.8,-15) rot=(0,0,1;0rad)
  Radius = 0.8
FEATURE [Part::Box] Box044  label="Cube042"
  Height = 4
  Length = 12
  Placement = pos=(-50,-16.75,-14) rot=(0,0,1;0rad)
  Width = 26.75
FEATURE [Part::Chamfer] Chamfer001
  Base = -> Box044
  Edges = 1 edges r=7: [Edge3]
FEATURE [Part::Cone] Cone002
  Angle = 360
  Height = 1.5
  Placement = pos=(-43.6,-2.4,-10) rot=(0,0,1;0rad)
  Radius1 = 2.75
  Radius2 = 1.25
FEATURE [Part::Cone] Cone003
  Angle = 360
  Height = 1.5
  Placement = pos=(-43.6,-13.8,-10) rot=(0,0,1;0rad)
  Radius1 = 2.75
  Radius2 = 1.25
FEATURE [Part::Fuse] Fusion114
  Base = -> Cone002
  Tool = -> Cone003
FEATURE [Part::Fuse] Fusion115
  Base = -> Chamfer001
  Tool = -> Fusion114
FEATURE [Part::Fuse] Fusion116
  Base = -> Cylinder081
  Tool = -> Cylinder082
FEATURE [Part::Cut] Cut045028
  Base = -> Fusion115
  Tool = -> Fusion116
FEATURE [Part::Mirroring] Part__Mirroring005  label="Cut045028 (Mirror #6)"
  Base = (0,0,0)
  Normal = (1,0,0)
  Placement = pos=(27,0,0) rot=(0,0,1;0rad)
  Source = -> Cut045028
